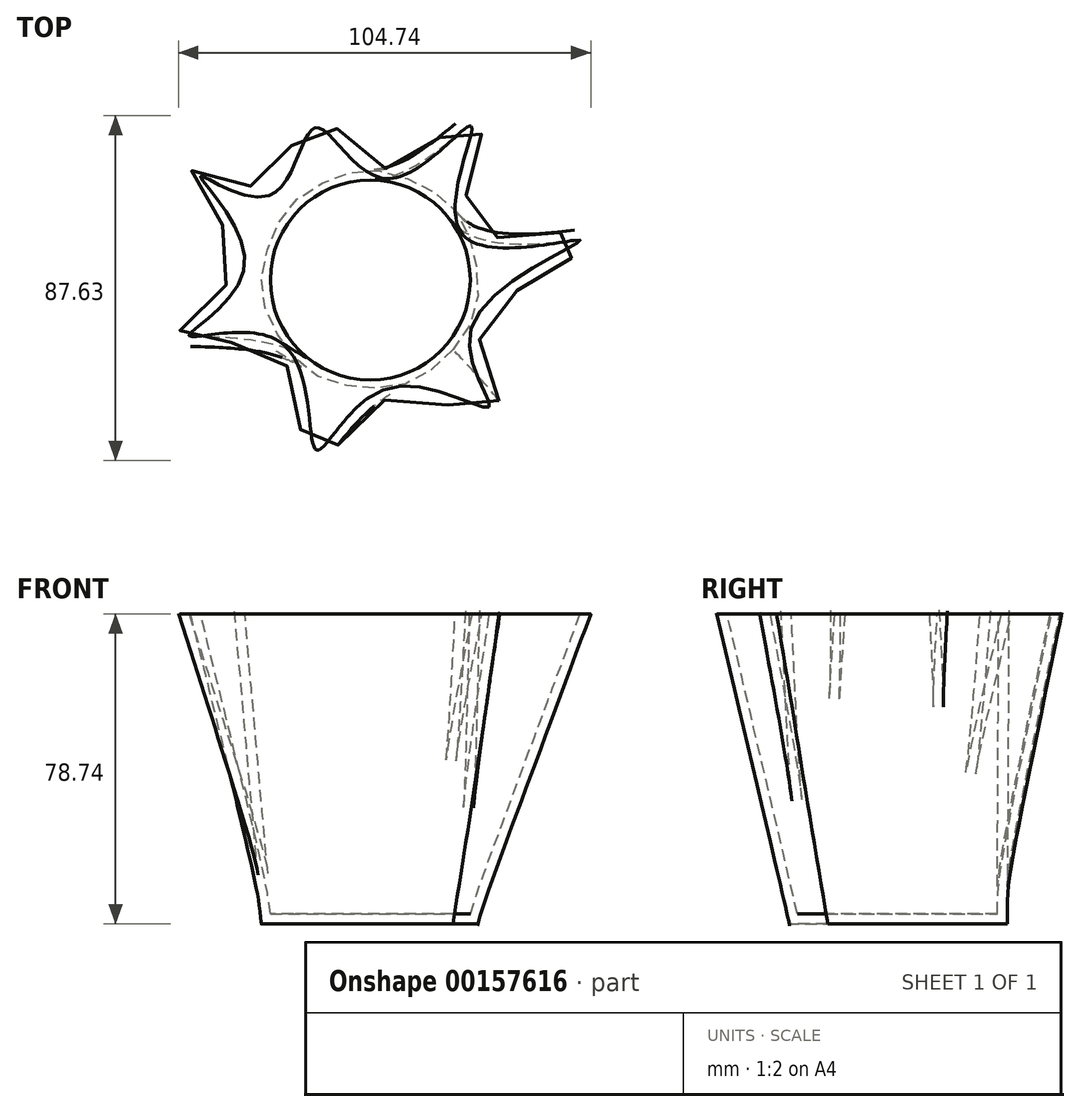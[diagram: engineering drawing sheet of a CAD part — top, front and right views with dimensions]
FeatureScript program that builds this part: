
annotation { "Feature Type Name" : "Feature", "Feature Type Description" : "" }
export const myFeature = defineFeature(function(context is Context, id is Id, definition is map)
    precondition{}
    {
        {
            var Q0;
            Q0=qCreatedBy(makeId("Top.planeOp"),FACE);
            var sketch = newSketch(context, id + "F0", { "sketchPlane" : qUnion([Q0])});
            skCircle(sketch, "E0", {"center": v(0, 0) * mm, "radius": 25.4 * mm});
            skSolve(sketch);
        }
        {
            var Q0;
            Q0=qCreatedBy(makeId("Top.planeOp"),FACE);
            cPlane(context, id + "F1", {"entities" : qUnion([Q0]), "cplaneType" : CPlaneType.OFFSET, "offset" : 76.2 * mm, "width" : 152.4 * mm, "height" : 152.4 * mm});
        }
        {
            var Q0;
            Q0=qCreatedBy(id+"F1.planeOp",FACE);
            var sketch = newSketch(context, id + "F2", { "sketchPlane" : qUnion([Q0])});
            skFitSpline(sketch, "E1", {"points": [v(-25.66, 21.45) * mm, v(-13.9, 38.68) * mm, v(4.3, 25.76) * mm, v(25.66, 39.07) * mm, v(23.5, 11.46) * mm, v(53.27, 10.09) * mm, v(25.85, -11.65) * mm, v(30.16, -32.22) * mm, v(4.3, -27.52) * mm, v(-13.71, -43.19) * mm, v(-22.33, -16.16) * mm, v(-46.03, -14.2) * mm, v(-31.93, 3.62) * mm, v(-43.09, 26.34) * mm, v(-25.66, 21.45) * mm]});
            skSolve(sketch);
        }
        {
            var Q0;
            Q0=makeQuery(id+"F2.imprint","IMPRINT",FACE,{"disambiguationData":[TD([[makeQuery(id+"F2.imprint","IMPRINT",EDGE,{"derivedFrom":sQuery(id+"F2.wireOp",EDGE,"E1")}),-1.0]])]});
            var Q1;
            Q1=makeQuery(id+"F0.imprint","IMPRINT",FACE,{"disambiguationData":[TD([[makeQuery(id+"F0.imprint","IMPRINT",EDGE,{"derivedFrom":sQuery(id+"F0.wireOp",EDGE,"E0")}),1.0]])]});
            loft(context, id + "F3", {"sheetProfilesArray" : [{ "sheetProfileEntities" : qUnion([Q0]) }, { "sheetProfileEntities" : qUnion([Q1]) }]});
        }
        {
            var Q0;
            Q0=makeQuery(id+"F3.opLoft","CAP_FACE",FACE,{"disambiguationData":[OSD([makeQuery(id+"F2.imprint","IMPRINT",FACE,{"disambiguationData":[TD([[makeQuery(id+"F2.imprint","IMPRINT",EDGE,{"derivedFrom":sQuery(id+"F2.wireOp",EDGE,"E1")}),-1.0]])]})])],"isStart":true});
            shell(context, id + "F4", {"entities" : qUnion([Q0]), "thickness" : 2.54 * mm, "oppositeDirection" : true});
        }
    });
